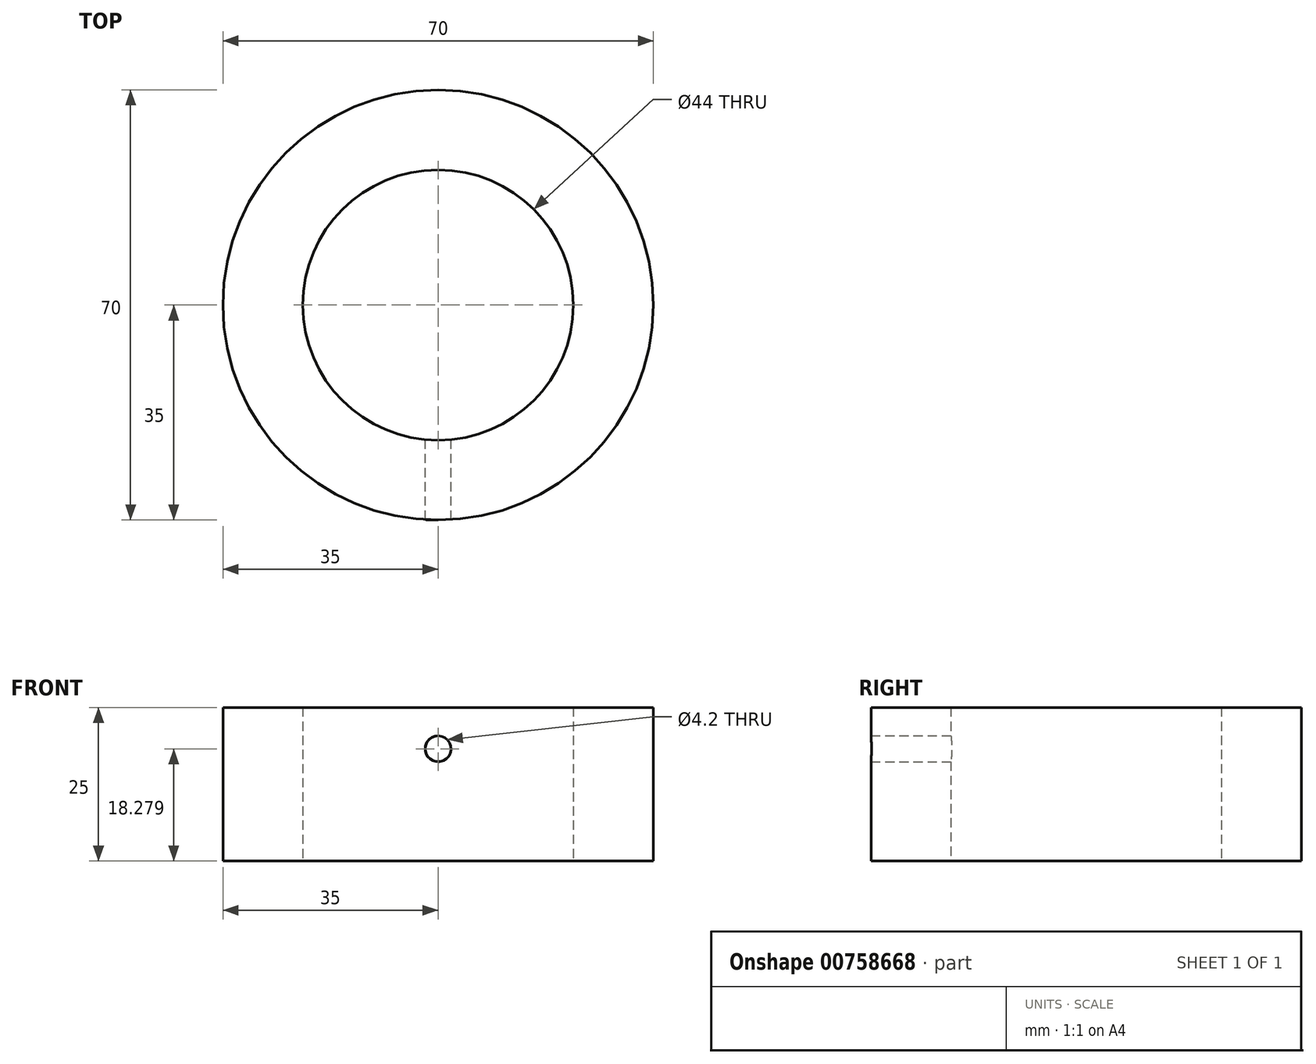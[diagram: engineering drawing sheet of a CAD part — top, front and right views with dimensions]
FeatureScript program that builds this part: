
annotation { "Feature Type Name" : "Feature", "Feature Type Description" : "" }
export const myFeature = defineFeature(function(context is Context, id is Id, definition is map)
    precondition{}
    {
        {
            var Q0;
            Q0=qCreatedBy(makeId("Top.planeOp"),FACE);
            var sketch = newSketch(context, id + "F0", { "sketchPlane" : qUnion([Q0])});
            skCircle(sketch, "E0", {"center": v(0, 0) * mm, "radius": 22 * mm});
            skCircle(sketch, "E1", {"center": v(0, 0) * mm, "radius": 35 * mm});
            skSolve(sketch);
        }
        {
            var Q0;
            Q0=makeQuery(id+"F0.imprint","IMPRINT",FACE,{"disambiguationData":[TD([[makeQuery(id+"F0.imprint","IMPRINT",EDGE,{"derivedFrom":sQuery(id+"F0.wireOp",EDGE,"E0")}),-1.0]])]});
            extrude(context, id + "F1", {"entities" : qUnion([Q0]), "depth" : 25 * mm, "offsetDistance" : 25 * mm});
        }
        {
            var Q0;
            Q0=qCreatedBy(makeId("Front.planeOp"),FACE);
            var sketch = newSketch(context, id + "F2", { "sketchPlane" : qUnion([Q0])});
            skPoint(sketch, "E2", {"position": v(0, 18.28) * mm});
            skSolve(sketch);
        }
        {
            var Q0;
            Q0=sQuery(id+"F2.wireOp",VERTEX,"E2");
            var Q1;
            Q1=makeQuery(id+"F1.opExtrude","SWEPT_BODY",BODY,{"disambiguationData":[OSD([sQuery(id+"F0.wireOp",EDGE,"E0"),sQuery(id+"F0.wireOp",EDGE,"E1")])]});
            hole(context, id + "F3", {"style" : HoleStyle.SIMPLE, "endStyle" : HoleEndStyle.THROUGH, "oppositeDirection" : true, "standardTappedOrClearance" : lookupTablePath({ "standard" : "ISO", "engagement" : "75%", "pitch" : "0.8 mm", "size" : "M5", "type" : "Tapped" }), "standardBlindInLast" : lookupTablePath({ "standard" : "ISO", "engagement" : "75%", "pitch" : "0.8 mm", "size" : "M5", "type" : "Tapped" }), "holeDiameter" : 4.2 * mm, "majorDiameter" : 5 * mm, "showTappedDepth" : true, "isTappedThrough" : true, "tappedDepth" : 12 * mm, "tapClearance" : 3, "locations" : qUnion([Q0]), "scope" : qUnion([Q1])});
        }
    });
